# Revit family: Plumbing Fixture-FloorDrain_Mifab_C1430
name_source: partatom
category: Plumbing Fixtures
revit_build: Autodesk Revit Structure 2013 (Build: 20120221_2030(x64)
units: mm (PartAtom-declared; Revit-internal decimal feet)

## types (7) — shared parameters
Description = RECESSED HEAD BRONZE LINE CLEANOUT PLUG
Floor Drain Material = Paint - Sherwin Williams Paint - #952C2A - Bellwood Red
Manufacturer = MIFAB
Model = C1430
URL = WWW.MIFAB.COM
zero-valued in all types: Default Elevation, WFU

## per-type parameters (varying)
| type | Body Height | Pipe Diameter | Pipe Radius | Stainer Diameter | Stainer Radius | Top Assembly Height |
| 2" | 6.5 " | 2 " | 1 " | 3 " | 1.5 " | 5.21 " |
| 2.5" | 6.5 " | 2.5 " | 1.25 " | 4 " | 2 " | 5.5 " |
| 3" | 6.5 " | 3 " | 1.5 " | 5 " | 2.5 " | 6 " |
| 4" | 7.5 " | 4 " | 2 " | 6 " | 3 " | 7 " |
| 5" | 12 " | 5 " | 2.5 " | 8 " | 4 " | 9 " |
| 6" | 12.5 " | 6 " | 3 " | 8 " | 4 " | 10 " |
| 8" | 14 " | 8 " | 4 " | 10 " | 5 " | 12 " |

## geometry (parser evidence)
native form markers: Blend x3, Sweep x1
no freeform markers — native parametric forms only
